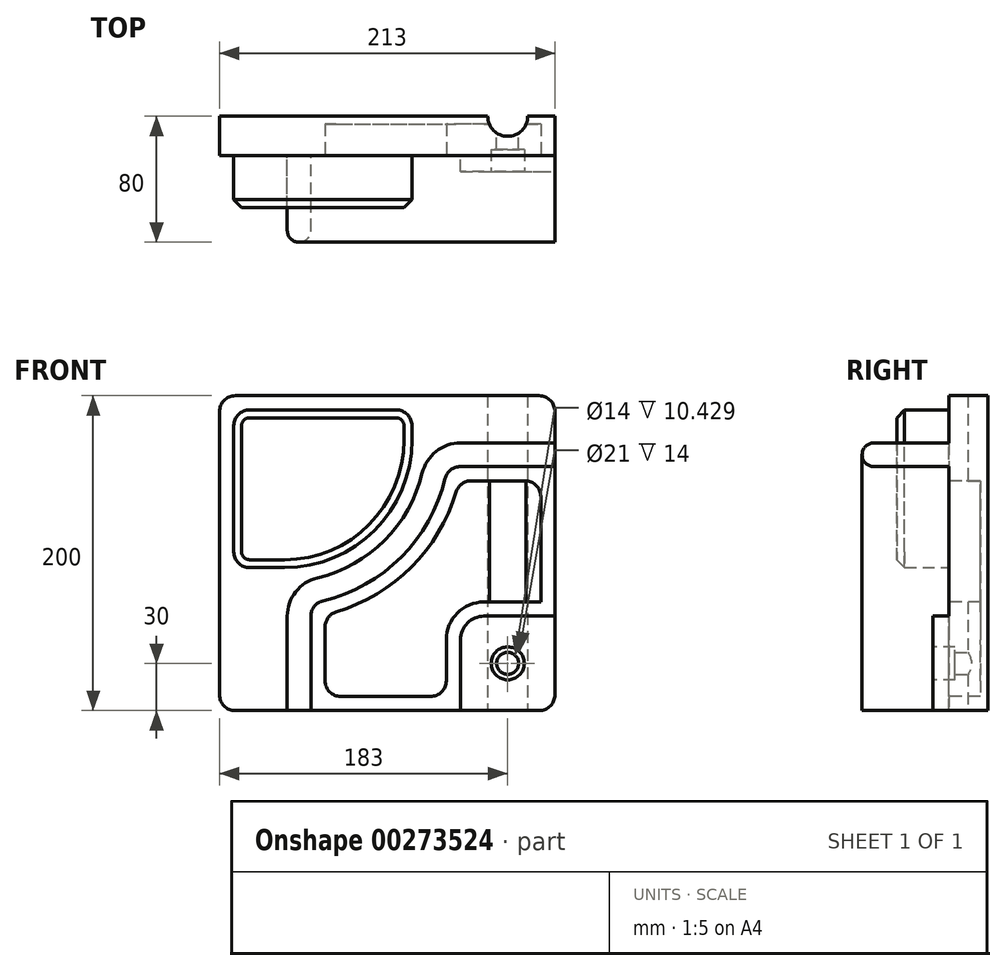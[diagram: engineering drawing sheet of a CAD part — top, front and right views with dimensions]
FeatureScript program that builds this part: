
annotation { "Feature Type Name" : "Feature", "Feature Type Description" : "" }
export const myFeature = defineFeature(function(context is Context, id is Id, definition is map)
    precondition{}
    {
        {
            var Q0;
            Q0=qCreatedBy(makeId("Front.planeOp"),FACE);
            var sketch = newSketch(context, id + "F0", { "sketchPlane" : qUnion([Q0])});
            skCircle(sketch, "E0", {"center": v(0, 0) * mm, "radius": 7 * mm});
            skLineSegment(sketch, "E1", {"start": v(-173, -30) * mm, "end": v(20, -30) * mm});
            skLineSegment(sketch, "E2", {"start": v(-183, -20) * mm, "end": v(-183, 160) * mm});
            skLineSegment(sketch, "E3", {"start": v(-173, 170) * mm, "end": v(20, 170) * mm});
            skLineSegment(sketch, "E4", {"start": v(30, 160) * mm, "end": v(30, -20) * mm});
            skPoint(sketch, "E5.visualSharp", {"position": v(-183, 170) * mm});
            skArc(sketch, "E5.filletArc", {"start": v(-173, 170) * mm, "mid": v(-180.07, 167.07) * mm, "end": v(-183, 160) * mm});
            skPoint(sketch, "E6.visualSharp", {"position": v(30, 170) * mm});
            skArc(sketch, "E6.filletArc", {"start": v(30, 160) * mm, "mid": v(27.07, 167.07) * mm, "end": v(20, 170) * mm});
            skPoint(sketch, "E7.visualSharp", {"position": v(30, -30) * mm});
            skArc(sketch, "E7.filletArc", {"start": v(20, -30) * mm, "mid": v(27.07, -27.07) * mm, "end": v(30, -20) * mm});
            skPoint(sketch, "E8.visualSharp", {"position": v(-183, -30) * mm});
            skArc(sketch, "E8.filletArc", {"start": v(-183, -20) * mm, "mid": v(-180.07, -27.07) * mm, "end": v(-173, -30) * mm});
            skSolve(sketch);
        }
        {
            var Q0;
            Q0 = qSketchRegion(id + "F0", true);
            extrude(context, id + "F1", {"entities" : qUnion([Q0]), "depth" : 25 * mm});
        }
        {
            var Q0;
            Q0=makeQuery(id+"F1.opExtrude","CAP_FACE",FACE,{"disambiguationData":[OSD([sQuery(id+"F0.wireOp",EDGE,"E0"),sQuery(id+"F0.wireOp",EDGE,"E1"),sQuery(id+"F0.wireOp",EDGE,"E2"),sQuery(id+"F0.wireOp",EDGE,"E3"),sQuery(id+"F0.wireOp",EDGE,"E4"),sQuery(id+"F0.wireOp",EDGE,"E5.filletArc"),sQuery(id+"F0.wireOp",EDGE,"E6.filletArc"),sQuery(id+"F0.wireOp",EDGE,"E7.filletArc"),sQuery(id+"F0.wireOp",EDGE,"E8.filletArc")])],"isStart":false});
            var sketch = newSketch(context, id + "F2", { "sketchPlane" : qUnion([Q0])});
            skLineSegment(sketch, "E9", {"start": v(-30, -30) * mm, "end": v(-30, 15) * mm});
            skLineSegment(sketch, "E10", {"start": v(-15, 30) * mm, "end": v(30, 30) * mm});
            skPoint(sketch, "E11.visualSharp", {"position": v(-30, 30) * mm});
            skArc(sketch, "E11.filletArc", {"start": v(-15, 30) * mm, "mid": v(-25.6, 25.6) * mm, "end": v(-30, 15) * mm});
            skLineSegment(sketch, "E12", {"start": v(-30, -30) * mm, "end": v(20, -30) * mm});
            skLineSegment(sketch, "E13", {"start": v(30, 30) * mm, "end": v(30, -20) * mm});
            skPoint(sketch, "E14.visualSharp", {"position": v(30, -30) * mm});
            skArc(sketch, "E14.filletArc", {"start": v(20, -30) * mm, "mid": v(27.07, -27.07) * mm, "end": v(30, -20) * mm});
            skSolve(sketch);
        }
        {
            var Q0;
            Q0 = qSketchRegion(id + "F2", true);
            extrude(context, id + "F3", {"entities" : qUnion([Q0]), "operationType" : NewBodyOperationType.ADD, "depth" : 10 * mm});
        }
        {
            var Q0;
            Q0=makeQuery(id+"F3.opExtrude","CAP_FACE",FACE,{"disambiguationData":[OSD([sQuery(id+"F2.wireOp",EDGE,"E9"),sQuery(id+"F2.wireOp",EDGE,"E10"),sQuery(id+"F2.wireOp",EDGE,"E11.filletArc"),sQuery(id+"F2.wireOp",EDGE,"E12"),sQuery(id+"F2.wireOp",EDGE,"E13"),sQuery(id+"F2.wireOp",EDGE,"E14.filletArc")])],"isStart":false});
            var sketch = newSketch(context, id + "F4", { "sketchPlane" : qUnion([Q0])});
            skCircle(sketch, "E15", {"center": v(0, 0) * mm, "radius": 10.5 * mm});
            skSolve(sketch);
        }
        {
            var Q0;
            Q0 = qSketchRegion(id + "F4", true);
            extrude(context, id + "F5", {"entities" : qUnion([Q0]), "operationType" : NewBodyOperationType.REMOVE, "oppositeDirection" : true, "depth" : 14 * mm});
        }
        {
            var Q0;
            Q0=makeQuery(id+"F1.opExtrude","CAP_FACE",FACE,{"disambiguationData":[OSD([sQuery(id+"F0.wireOp",EDGE,"E0"),sQuery(id+"F0.wireOp",EDGE,"E1"),sQuery(id+"F0.wireOp",EDGE,"E2"),sQuery(id+"F0.wireOp",EDGE,"E3"),sQuery(id+"F0.wireOp",EDGE,"E4"),sQuery(id+"F0.wireOp",EDGE,"E5.filletArc"),sQuery(id+"F0.wireOp",EDGE,"E6.filletArc"),sQuery(id+"F0.wireOp",EDGE,"E7.filletArc"),sQuery(id+"F0.wireOp",EDGE,"E8.filletArc")])],"isStart":false});
            var sketch = newSketch(context, id + "F6", { "sketchPlane" : qUnion([Q0])});
            skLineSegment(sketch, "E16", {"start": v(-140, -30) * mm, "end": v(-140, 30) * mm});
            skLineSegment(sketch, "E17", {"start": v(30, 140) * mm, "end": v(-30, 140) * mm});
            skArc(sketch, "E18", {"start": v(-120.83, 54.31) * mm, "mid": v(-134.63, 45.48) * mm, "end": v(-140, 30) * mm});
            skArc(sketch, "E19", {"start": v(-30, 140) * mm, "mid": v(-45.48, 134.63) * mm, "end": v(-54.31, 120.83) * mm});
            skArc(sketch, "E20", {"start": v(-120.83, 54.31) * mm, "mid": v(-78.19, 78.19) * mm, "end": v(-54.31, 120.83) * mm});
            skLineSegment(sketch, "E21.0", {"start": v(30, 125) * mm, "end": v(-30, 125) * mm});
            skLineSegment(sketch, "E21.1", {"start": v(-125, -30) * mm, "end": v(-125, 30) * mm});
            skArc(sketch, "E21.2", {"start": v(-117.33, 39.72) * mm, "mid": v(-122.85, 36.2) * mm, "end": v(-125, 30) * mm});
            skArc(sketch, "E21.3", {"start": v(-117.33, 39.72) * mm, "mid": v(-67.58, 67.58) * mm, "end": v(-39.72, 117.33) * mm});
            skArc(sketch, "E21.4", {"start": v(-30, 125) * mm, "mid": v(-36.2, 122.85) * mm, "end": v(-39.72, 117.33) * mm});
            skLineSegment(sketch, "E22", {"start": v(-140, -30) * mm, "end": v(-125, -30) * mm});
            skLineSegment(sketch, "E23", {"start": v(30, 140) * mm, "end": v(30, 125) * mm});
            skSolve(sketch);
        }
        {
            var Q0;
            Q0 = qSketchRegion(id + "F6", true);
            extrude(context, id + "F7", {"entities" : qUnion([Q0]), "operationType" : NewBodyOperationType.ADD, "depth" : 55 * mm});
        }
        {
            var Q0;
            Q0=makeQuery(id+"F7.opExtrude","CAP_EDGE",EDGE,{"disambiguationData":[OSD([sQuery(id+"F6.wireOp",EDGE,"E21.1")])],"isStart":false});
            var Q1;
            Q1=makeQuery(id+"F7.opExtrude","CAP_EDGE",EDGE,{"disambiguationData":[OSD([sQuery(id+"F6.wireOp",EDGE,"E16")])],"isStart":false});
            fillet(context, id + "F8", {"entities" : qUnion([Q0, Q1]), "radius" : 7.5 * mm, "tangentPropagation" : true, "allowEdgeOverflow" : false});
        }
        {
            var Q0;
            {var subQ0=sQuery(id+"F0.wireOp",EDGE,"E1");var subQ1=sQuery(id+"F0.wireOp",EDGE,"E4");Q0=makeQuery(id+"F7.boolean.opBoolean","SPLIT",FACE,{"disambiguationData":[TD([makeQuery(id+"F3.opExtrude","SWEPT_FACE",FACE,{"disambiguationData":[OSD([sQuery(id+"F2.wireOp",EDGE,"E9")])]})])],"derivedFrom":makeQuery(id+"F1.opExtrude","CAP_FACE",FACE,{"disambiguationData":[OSD([sQuery(id+"F0.wireOp",EDGE,"E0"),subQ0,sQuery(id+"F0.wireOp",EDGE,"E2"),sQuery(id+"F0.wireOp",EDGE,"E3"),subQ1,sQuery(id+"F0.wireOp",EDGE,"E5.filletArc"),sQuery(id+"F0.wireOp",EDGE,"E6.filletArc"),sQuery(id+"F0.wireOp",EDGE,"E7.filletArc"),sQuery(id+"F0.wireOp",EDGE,"E8.filletArc")])],"isStart":false})});}
            var sketch = newSketch(context, id + "F9", { "sketchPlane" : qUnion([Q0])});
            skLineSegment(sketch, "E24.0", {"start": v(-116, 23.12) * mm, "end": v(-116, -11) * mm});
            skLineSegment(sketch, "E24.1", {"start": v(11, 116) * mm, "end": v(-23.12, 116) * mm});
            skLineSegment(sketch, "E25", {"start": v(-106, -21) * mm, "end": v(-49, -21) * mm});
            skLineSegment(sketch, "E26", {"start": v(-39, -11) * mm, "end": v(-39, 15) * mm});
            skLineSegment(sketch, "E27", {"start": v(-15, 39) * mm, "end": v(21, 39) * mm});
            skLineSegment(sketch, "E28", {"start": v(21, 39) * mm, "end": v(21, 106) * mm});
            skPoint(sketch, "E29.0.start.orphan", {"position": v(30, 125) * mm});
            skArc(sketch, "E30.filletArc", {"start": v(21, 106) * mm, "mid": v(18.07, 113.07) * mm, "end": v(11, 116) * mm});
            skArc(sketch, "E31.filletArc", {"start": v(-23.12, 116) * mm, "mid": v(-29.08, 114.03) * mm, "end": v(-32.69, 108.89) * mm});
            skArc(sketch, "E32.filletArc", {"start": v(-108.89, 32.69) * mm, "mid": v(-114.03, 29.08) * mm, "end": v(-116, 23.12) * mm});
            skArc(sketch, "E33.filletArc", {"start": v(-116, -11) * mm, "mid": v(-113.07, -18.07) * mm, "end": v(-106, -21) * mm});
            skPoint(sketch, "E34.visualSharp", {"position": v(-39, -21) * mm});
            skArc(sketch, "E34.filletArc", {"start": v(-49, -21) * mm, "mid": v(-41.93, -18.07) * mm, "end": v(-39, -11) * mm});
            skArc(sketch, "E35.0", {"start": v(-15, 39) * mm, "mid": v(-31.97, 31.97) * mm, "end": v(-39, 15) * mm});
            skArc(sketch, "E36.0", {"start": v(-32.69, 108.89) * mm, "mid": v(-61.22, 61.22) * mm, "end": v(-108.89, 32.69) * mm});
            skSolve(sketch);
        }
        {
            var Q0;
            Q0 = qSketchRegion(id + "F9", true);
            extrude(context, id + "F10", {"entities" : qUnion([Q0]), "operationType" : NewBodyOperationType.REMOVE, "oppositeDirection" : true, "depth" : 20 * mm});
        }
        {
            var Q0;
            {var subQ0=sQuery(id+"F0.wireOp",EDGE,"E6.filletArc");var subQ1=sQuery(id+"F0.wireOp",EDGE,"E5.filletArc");var subQ2=sQuery(id+"F0.wireOp",EDGE,"E8.filletArc");var subQ3=sQuery(id+"F0.wireOp",EDGE,"E1");var subQ4=sQuery(id+"F0.wireOp",EDGE,"E2");var subQ5=sQuery(id+"F0.wireOp",EDGE,"E3");var subQ6=sQuery(id+"F0.wireOp",EDGE,"E4");Q0=makeQuery(id+"F7.boolean.opBoolean","SPLIT",FACE,{"disambiguationData":[TD([makeQuery(id+"F1.opExtrude","SWEPT_FACE",FACE,{"disambiguationData":[OSD([subQ4])]})])],"derivedFrom":makeQuery(id+"F1.opExtrude","CAP_FACE",FACE,{"disambiguationData":[OSD([sQuery(id+"F0.wireOp",EDGE,"E0"),subQ3,subQ4,subQ5,subQ6,subQ1,subQ0,sQuery(id+"F0.wireOp",EDGE,"E7.filletArc"),subQ2])],"isStart":false})});}
            var sketch = newSketch(context, id + "F11", { "sketchPlane" : qUnion([Q0])});
            skLineSegment(sketch, "E37", {"start": v(-164, 161) * mm, "end": v(-70.83, 161) * mm});
            skLineSegment(sketch, "E38", {"start": v(-174, 151) * mm, "end": v(-174, 70.83) * mm});
            skArc(sketch, "E39", {"start": v(-141.83, 60.83) * mm, "mid": v(-84.55, 84.55) * mm, "end": v(-60.83, 141.83) * mm});
            skLineSegment(sketch, "E40", {"start": v(-164, 60.83) * mm, "end": v(-141.83, 60.83) * mm});
            skLineSegment(sketch, "E41", {"start": v(-60.83, 141.83) * mm, "end": v(-60.83, 151) * mm});
            skPoint(sketch, "E42.visualSharp", {"position": v(-174, 161) * mm});
            skArc(sketch, "E42.filletArc", {"start": v(-164, 161) * mm, "mid": v(-171.07, 158.07) * mm, "end": v(-174, 151) * mm});
            skPoint(sketch, "E43.visualSharp", {"position": v(-60.83, 161) * mm});
            skArc(sketch, "E43.filletArc", {"start": v(-60.83, 151) * mm, "mid": v(-63.76, 158.07) * mm, "end": v(-70.83, 161) * mm});
            skPoint(sketch, "E44.visualSharp", {"position": v(-174, 60.83) * mm});
            skArc(sketch, "E44.filletArc", {"start": v(-174, 70.83) * mm, "mid": v(-171.07, 63.76) * mm, "end": v(-164, 60.83) * mm});
            skSolve(sketch);
        }
        {
            var Q0;
            Q0 = qSketchRegion(id + "F11", true);
            extrude(context, id + "F12", {"entities" : qUnion([Q0]), "operationType" : NewBodyOperationType.ADD, "depth" : 33 * mm});
        }
        {
            var Q0;
            Q0=makeQuery(id+"F12.opExtrude","CAP_EDGE",EDGE,{"disambiguationData":[OSD([sQuery(id+"F11.wireOp",EDGE,"E38")])],"isStart":false});
            chamfer(context, id + "F13", {"entities" : qUnion([Q0]), "chamferType" : ChamferType.OFFSET_ANGLE, "width" : 5 * mm, "oppositeDirection" : false, "angle" : 45 * degree, "tangentPropagation" : true});
        }
        {
            var Q0;
            Q0=makeQuery(id+"F7.boolean.opBoolean","MERGE",FACE,{"derivedFrom":[makeQuery(id+"F3.boolean.opBoolean","MERGE",FACE,{"derivedFrom":[makeQuery(id+"F1.opExtrude","SWEPT_FACE",FACE,{"disambiguationData":[OSD([sQuery(id+"F0.wireOp",EDGE,"E1")])]}),makeQuery(id+"F3.opExtrude","SWEPT_FACE",FACE,{"disambiguationData":[OSD([sQuery(id+"F2.wireOp",EDGE,"E12")])]})]}),makeQuery(id+"F7.opExtrude","SWEPT_FACE",FACE,{"disambiguationData":[OSD([sQuery(id+"F6.wireOp",EDGE,"E22")])]})]});
            var sketch = newSketch(context, id + "F14", { "sketchPlane" : qUnion([Q0])});
            skArc(sketch, "E45", {"start": v(12.68, 0) * mm, "mid": v(0, 12.68) * mm, "end": v(-12.68, 0) * mm});
            skLineSegment(sketch, "E46", {"start": v(-12.68, 0) * mm, "end": v(12.68, 0) * mm});
            skSolve(sketch);
        }
        {
            var Q0;
            Q0 = qSketchRegion(id + "F14", true);
            extrude(context, id + "F15", {"entities" : qUnion([Q0]), "operationType" : NewBodyOperationType.REMOVE, "oppositeDirection" : true, "depth" : 400 * mm});
        }
    });
